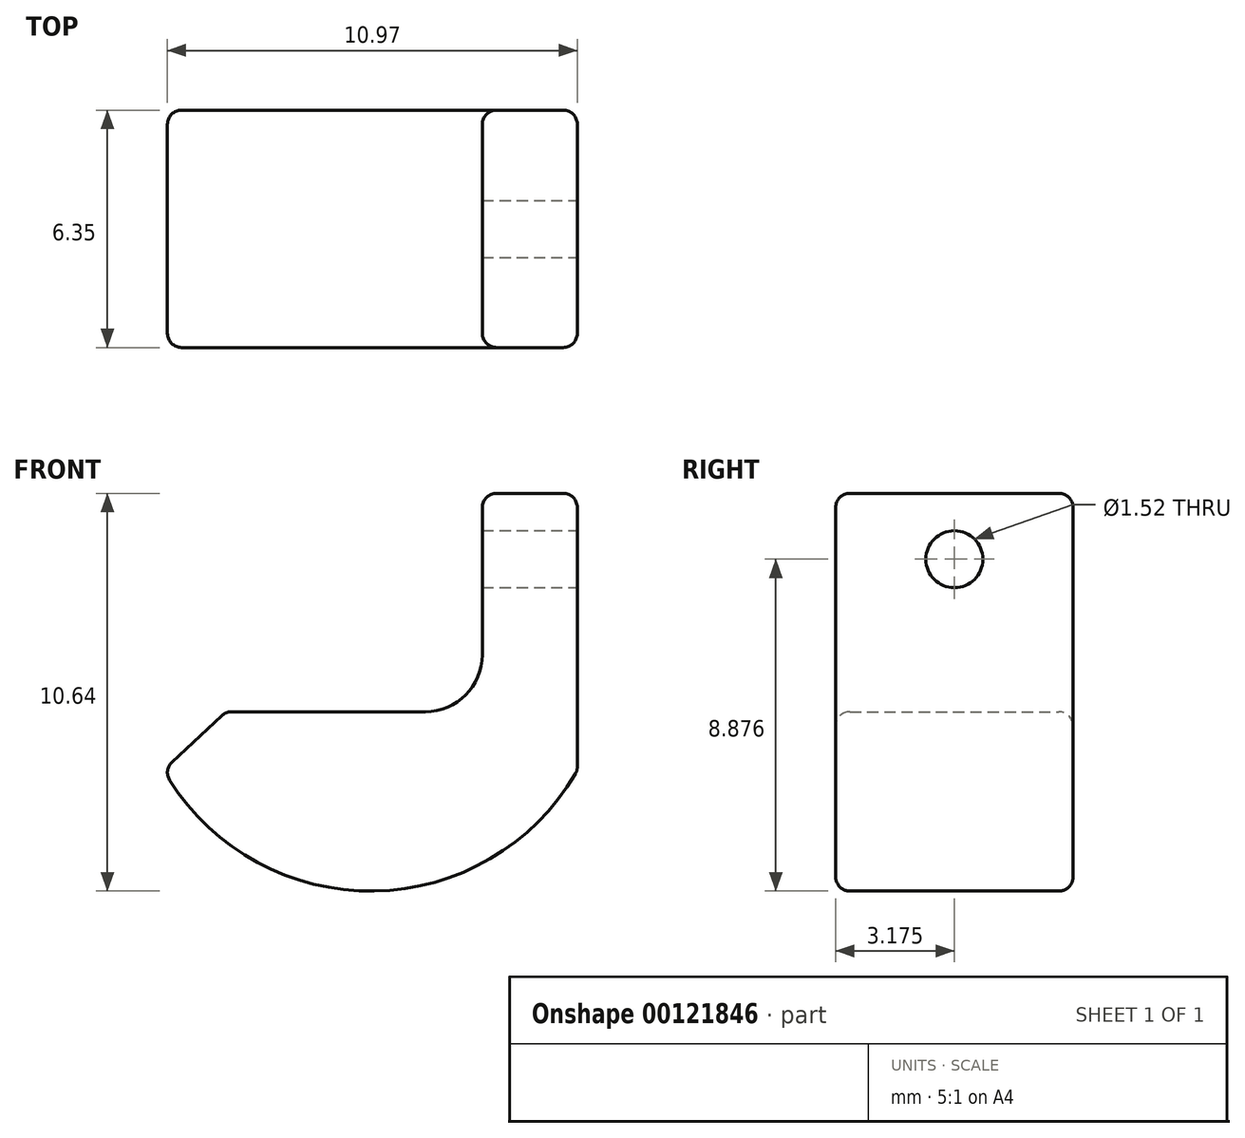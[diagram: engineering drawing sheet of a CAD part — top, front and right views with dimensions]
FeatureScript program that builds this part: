
annotation { "Feature Type Name" : "Feature", "Feature Type Description" : "" }
export const myFeature = defineFeature(function(context is Context, id is Id, definition is map)
    precondition{}
    {
        {
            var Q0;
            Q0=qCreatedBy(makeId("Front.planeOp"),FACE);
            var sketch = newSketch(context, id + "F0", { "sketchPlane" : qUnion([Q0])});
            skLineSegment(sketch, "E0", {"start": v(0, 0) * mm, "end": v(0, -7.4) * mm});
            skLineSegment(sketch, "E1.0", {"start": v(-2.54, 0) * mm, "end": v(-2.54, -4.32) * mm});
            skLineSegment(sketch, "E2", {"start": v(-2.54, 0) * mm, "end": v(0, 0) * mm});
            skLineSegment(sketch, "E3", {"start": v(-4.06, -5.84) * mm, "end": v(-9.4, -5.84) * mm});
            skPoint(sketch, "E4.visualSharp", {"position": v(-2.54, -5.84) * mm});
            skArc(sketch, "E4.filletArc", {"start": v(-4.06, -5.84) * mm, "mid": v(-2.99, -5.4) * mm, "end": v(-2.54, -4.32) * mm});
            skLineSegment(sketch, "E5", {"start": v(-9.4, -5.84) * mm, "end": v(-11.07, -7.4) * mm});
            skArc(sketch, "E6", {"start": v(-11.07, -7.4) * mm, "mid": v(-5.54, -10.64) * mm, "end": v(0, -7.4) * mm});
            skSolve(sketch);
        }
        {
            var Q0;
            Q0=makeQuery(id+"F0.imprint","IMPRINT",FACE,{"disambiguationData":[TD([[makeQuery(id+"F0.imprint","IMPRINT",EDGE,{"derivedFrom":sQuery(id+"F0.wireOp",EDGE,"E0")}),-1.0]])]});
            extrude(context, id + "F1", {"entities" : qUnion([Q0]), "depth" : 6.35 * mm});
        }
        {
            var Q0;
            Q0=makeQuery(id+"F1.opExtrude","SWEPT_FACE",FACE,{"disambiguationData":[OSD([sQuery(id+"F0.wireOp",EDGE,"E0"),sQuery(id+"F0.wireOp",EDGE,"II5cVi24-zZxF-bLCh-npmQ-r9aBbYHbcqHr")])]});
            var sketch = newSketch(context, id + "F2", { "sketchPlane" : qUnion([Q0])});
            skLineSegment(sketch, "E7.bottom", {"start": v(-1.14, -2.53) * mm, "end": v(-5.2, -2.53) * mm});
            skLineSegment(sketch, "E7.top", {"start": v(-1.14, -1) * mm, "end": v(-5.2, -1) * mm});
            skLineSegment(sketch, "E7.left", {"start": v(-1.14, -2.53) * mm, "end": v(-1.14, -1) * mm});
            skLineSegment(sketch, "E7.right", {"start": v(-5.2, -2.53) * mm, "end": v(-5.2, -1) * mm});
            skPoint(sketch, "E7.middle", {"position": v(-3.18, -1.76) * mm});
            skSolve(sketch);
        }
        {
            var Q0;
            Q0=sQuery(id+"F2.wireOp",VERTEX,"E7.middle");
            var Q1;
            Q1=makeQuery(id+"F1.opExtrude","SWEPT_BODY",BODY,{"disambiguationData":[OSD([sQuery(id+"F0.wireOp",EDGE,"E0"),sQuery(id+"F0.wireOp",EDGE,"E1.0"),sQuery(id+"F0.wireOp",EDGE,"E2"),sQuery(id+"F0.wireOp",EDGE,"E3"),sQuery(id+"F0.wireOp",EDGE,"E4.filletArc"),sQuery(id+"F0.wireOp",EDGE,"E5"),sQuery(id+"F0.wireOp",EDGE,"E6"),sQuery(id+"F0.wireOp",EDGE,"II5cVi24-zZxF-bLCh-npmQ-r9aBbYHbcqHr")])]});
            hole(context, id + "F3", {"style" : HoleStyle.SIMPLE, "endStyle" : HoleEndStyle.THROUGH, "holeDiameter" : 1.52 * mm, "locations" : qUnion([Q0]), "scope" : qUnion([Q1]), "isTappedThrough" : true});
        }
        {
            var Q0;
            Q0=makeQuery(id+"F1.opExtrude","SWEPT_EDGE",EDGE,{"disambiguationData":[OSD([sQuery(id+"F0.wireOp",EDGE,"E1.0"),sQuery(id+"F0.wireOp",EDGE,"E2")])]});
            var Q1;
            Q1=makeQuery(id+"F1.opExtrude","SWEPT_EDGE",EDGE,{"disambiguationData":[OSD([sQuery(id+"F0.wireOp",EDGE,"E0"),sQuery(id+"F0.wireOp",EDGE,"E2")])]});
            var Q2;
            Q2=makeQuery(id+"F1.opExtrude","CAP_EDGE",EDGE,{"disambiguationData":[OSD([sQuery(id+"F0.wireOp",EDGE,"E2")])],"isStart":false});
            var Q3;
            Q3=makeQuery(id+"F1.opExtrude","CAP_EDGE",EDGE,{"disambiguationData":[OSD([sQuery(id+"F0.wireOp",EDGE,"E2")])],"isStart":true});
            var Q4;
            Q4=makeQuery(id+"F1.opExtrude","CAP_EDGE",EDGE,{"disambiguationData":[OSD([sQuery(id+"F0.wireOp",EDGE,"E0")])],"isStart":false});
            var Q5;
            Q5=makeQuery(id+"F1.opExtrude","CAP_EDGE",EDGE,{"disambiguationData":[OSD([sQuery(id+"F0.wireOp",EDGE,"E1.0")])],"isStart":false});
            var Q6;
            Q6=makeQuery(id+"F1.opExtrude","CAP_EDGE",EDGE,{"disambiguationData":[OSD([sQuery(id+"F0.wireOp",EDGE,"E4.filletArc")])],"isStart":false});
            var Q7;
            Q7=makeQuery(id+"F1.opExtrude","CAP_EDGE",EDGE,{"disambiguationData":[OSD([sQuery(id+"F0.wireOp",EDGE,"E3")])],"isStart":false});
            var Q8;
            Q8=makeQuery(id+"F1.opExtrude","CAP_EDGE",EDGE,{"disambiguationData":[OSD([sQuery(id+"F0.wireOp",EDGE,"E5")])],"isStart":false});
            var Q9;
            Q9=makeQuery(id+"F1.opExtrude","CAP_EDGE",EDGE,{"disambiguationData":[OSD([sQuery(id+"F0.wireOp",EDGE,"E6")])],"isStart":false});
            var Q10;
            Q10=makeQuery(id+"F1.opExtrude","SWEPT_EDGE",EDGE,{"disambiguationData":[OSD([sQuery(id+"F0.wireOp",EDGE,"E0"),sQuery(id+"F0.wireOp",EDGE,"E6")])]});
            var Q11;
            Q11=makeQuery(id+"F1.opExtrude","SWEPT_EDGE",EDGE,{"disambiguationData":[OSD([sQuery(id+"F0.wireOp",EDGE,"E3"),sQuery(id+"F0.wireOp",EDGE,"E5")])]});
            var Q12;
            Q12=makeQuery(id+"F1.opExtrude","CAP_EDGE",EDGE,{"disambiguationData":[OSD([sQuery(id+"F0.wireOp",EDGE,"E1.0")])],"isStart":true});
            var Q13;
            Q13=makeQuery(id+"F1.opExtrude","CAP_EDGE",EDGE,{"disambiguationData":[OSD([sQuery(id+"F0.wireOp",EDGE,"E4.filletArc")])],"isStart":true});
            var Q14;
            Q14=makeQuery(id+"F1.opExtrude","CAP_EDGE",EDGE,{"disambiguationData":[OSD([sQuery(id+"F0.wireOp",EDGE,"E3")])],"isStart":true});
            var Q15;
            Q15=makeQuery(id+"F1.opExtrude","CAP_EDGE",EDGE,{"disambiguationData":[OSD([sQuery(id+"F0.wireOp",EDGE,"E5")])],"isStart":true});
            var Q16;
            Q16=makeQuery(id+"F1.opExtrude","CAP_EDGE",EDGE,{"disambiguationData":[OSD([sQuery(id+"F0.wireOp",EDGE,"E6")])],"isStart":true});
            var Q17;
            Q17=makeQuery(id+"F1.opExtrude","CAP_EDGE",EDGE,{"disambiguationData":[OSD([sQuery(id+"F0.wireOp",EDGE,"E0")])],"isStart":true});
            var Q18;
            Q18=makeQuery(id+"F3.hole-0.boolean.opBoolean","INTERSECT",EDGE,{"derivedFrom":[makeQuery(id+"F1.opExtrude","SWEPT_FACE",FACE,{"disambiguationData":[OSD([sQuery(id+"F0.wireOp",EDGE,"E1.0")])]}),makeQuery(id+"F3.hole-0.opRevolve","SWEPT_FACE",FACE,{"disambiguationData":[OSD([sQuery(id+"F3.hole-0.sketch.wireOp",EDGE,"core_line_2")])]})]});
            var Q19;
            Q19=makeQuery(id+"F1.opExtrude","SWEPT_EDGE",EDGE,{"disambiguationData":[OSD([sQuery(id+"F0.wireOp",EDGE,"E5"),sQuery(id+"F0.wireOp",EDGE,"E6")])]});
            var Q20;
            Q20=makeQuery(id+"F3.hole-0.boolean.opBoolean","COPY",EDGE,{"derivedFrom":makeQuery(id+"F3.hole-0.opRevolve","SWEPT_EDGE",EDGE,{"disambiguationData":[OSD([sQuery(id+"F3.hole-0.sketch.wireOp",EDGE,"core_line_2"),sQuery(id+"F3.hole-0.sketch.wireOp",EDGE,"core_line_3")])]})});
            fillet(context, id + "F4", {"entities" : qUnion([Q0, Q1, Q2, Q3, Q4, Q5, Q6, Q7, Q8, Q9, Q10, Q11, Q12, Q13, Q14, Q15, Q16, Q17, Q18, Q19, Q20]), "radius" : 0.38 * mm, "allowEdgeOverflow" : false});
        }
    });
